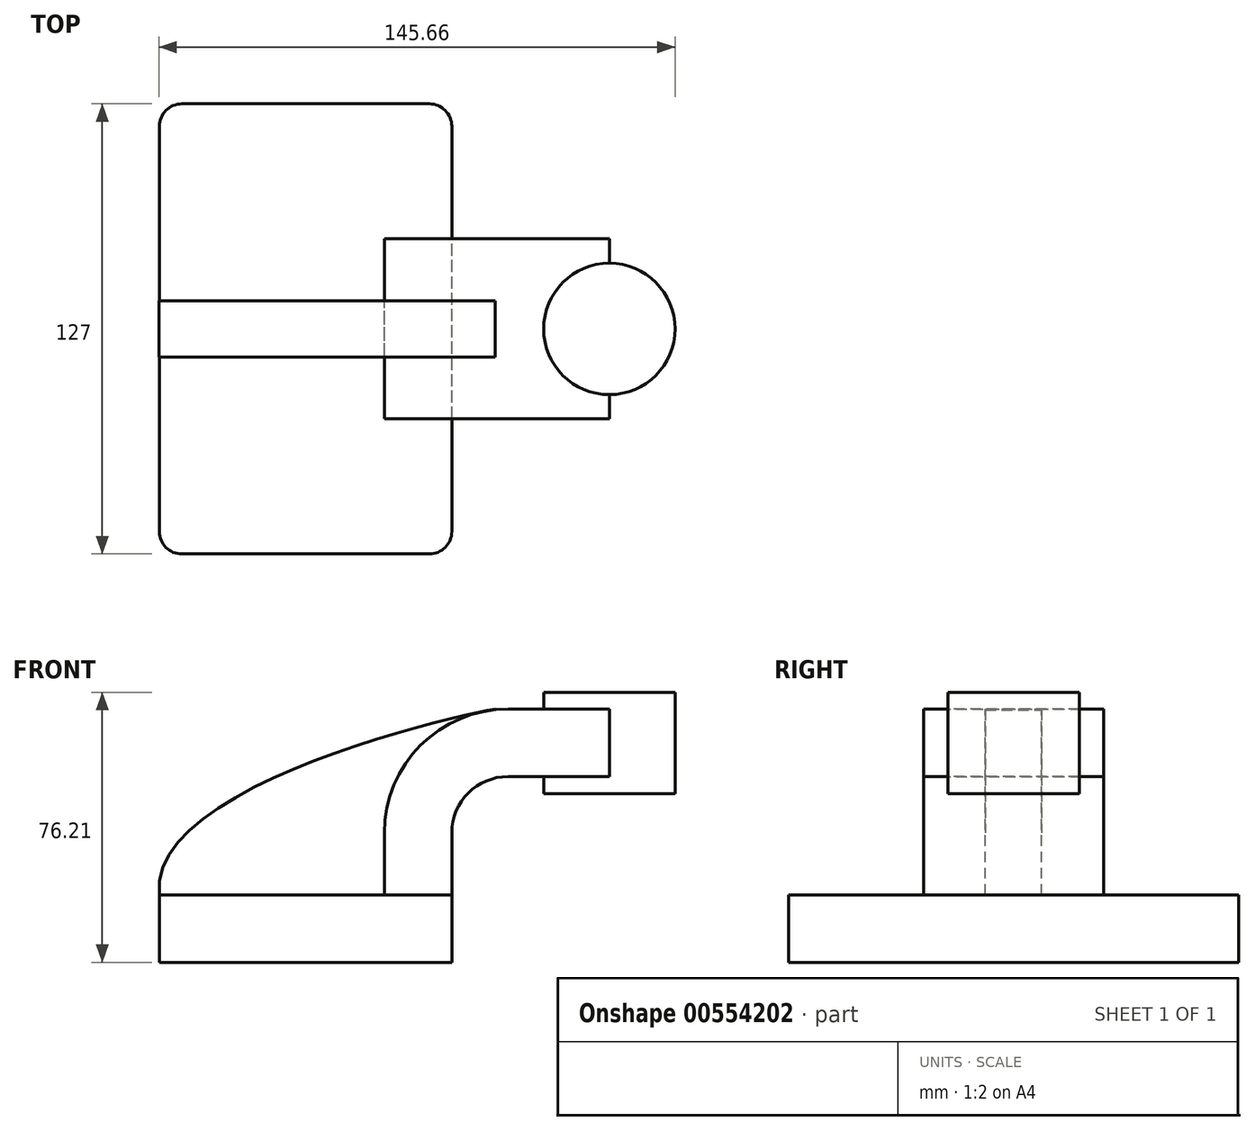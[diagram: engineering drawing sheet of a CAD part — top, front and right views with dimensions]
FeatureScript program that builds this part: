
annotation { "Feature Type Name" : "Feature", "Feature Type Description" : "" }
export const myFeature = defineFeature(function(context is Context, id is Id, definition is map)
    precondition{}
    {
        {
            var Q0;
            Q0=qCreatedBy(makeId("Front.planeOp"),FACE);
            var sketch = newSketch(context, id + "F0", { "sketchPlane" : qUnion([Q0])});
            skLineSegment(sketch, "E0.bottom", {"start": v(-41.28, 9.52) * mm, "end": v(41.27, 9.53) * mm});
            skLineSegment(sketch, "E0.top", {"start": v(-41.28, -9.53) * mm, "end": v(41.28, -9.53) * mm});
            skLineSegment(sketch, "E0.left", {"start": v(-41.28, 9.52) * mm, "end": v(-41.28, -9.53) * mm});
            skLineSegment(sketch, "E0.right", {"start": v(41.27, 9.53) * mm, "end": v(41.28, -9.52) * mm});
            skPoint(sketch, "E0.middle", {"position": v(0, 0) * mm});
            skLineSegment(sketch, "E1.bottom", {"start": v(104.27, 38.1) * mm, "end": v(53.47, 38.1) * mm});
            skLineSegment(sketch, "E1.top", {"start": v(104.27, 66.67) * mm, "end": v(53.47, 66.67) * mm});
            skLineSegment(sketch, "E1.left", {"start": v(104.27, 38.1) * mm, "end": v(104.27, 66.67) * mm});
            skLineSegment(sketch, "E1.right", {"start": v(53.47, 38.1) * mm, "end": v(53.47, 66.67) * mm});
            skPoint(sketch, "E1.middle", {"position": v(78.87, 52.39) * mm});
            skLineSegment(sketch, "E2", {"start": v(41.27, 9.53) * mm, "end": v(41.27, 27) * mm});
            skArc(sketch, "E3", {"start": v(41.27, 27) * mm, "mid": v(45.92, 38.23) * mm, "end": v(57.15, 42.88) * mm});
            skLineSegment(sketch, "E4", {"start": v(57.15, 42.88) * mm, "end": v(85.72, 42.88) * mm});
            skLineSegment(sketch, "E5.0", {"start": v(57.15, 61.93) * mm, "end": v(85.72, 61.93) * mm});
            skArc(sketch, "E5.1", {"start": v(22.22, 27) * mm, "mid": v(32.45, 51.7) * mm, "end": v(57.15, 61.93) * mm});
            skLineSegment(sketch, "E5.2", {"start": v(22.22, 9.53) * mm, "end": v(22.22, 27) * mm});
            skLineSegment(sketch, "E6", {"start": v(85.72, 42.88) * mm, "end": v(85.72, 61.93) * mm});
            skFitSpline(sketch, "E7", {"points": [v(-41.28, 9.52) * mm, v(53.47, 61.93) * mm, v(57.15, 61.93) * mm], "startDerivative": vector(-12.96, 107.01) * mm, "endDerivative": vector(16.74, -4.83) * mm});
            skLineSegment(sketch, "E8", {"start": v(85.72, 42.88) * mm, "end": v(85.72, 38.1) * mm});
            skPoint(sketch, "E8.endSnap0", {"position": v(78.87, 38.1) * mm});
            skLineSegment(sketch, "E9", {"start": v(85.72, 61.93) * mm, "end": v(85.72, 66.67) * mm});
            skSolve(sketch);
        }
        {
            var Q0;
            Q0=makeQuery(id+"F0.imprint","IMPRINT",FACE,{"disambiguationData":[TD([[makeQuery(id+"F0.imprint","IMPRINT",EDGE,{"derivedFrom":sQuery(id+"F0.wireOp",EDGE,"E0.top")}),1.0]])]});
            extrude(context, id + "F1", {"entities" : qUnion([Q0]), "endBound" : BoundingType.SYMMETRIC, "depth" : 127 * mm, "offsetDistance" : 25.4 * mm});
        }
        {
            var Q0;
            {var subQ1=sQuery(id+"F0.wireOp",EDGE,"E2");Q0=makeQuery(id+"F0.imprint","IMPRINT",FACE,{"disambiguationData":[TD([[makeQuery(id+"F0.imprint","IMPRINT",EDGE,{"derivedFrom":subQ1}),1.0]])]});}
            var Q1;
            {var subQ1=sQuery(id+"F0.wireOp",EDGE,"E4");Q1=makeQuery(id+"F0.imprint","IMPRINT",FACE,{"disambiguationData":[TD([[makeQuery(id+"F0.imprint","IMPRINT",EDGE,{"derivedFrom":subQ1}),1.0]])]});}
            extrude(context, id + "F2", {"entities" : qUnion([Q0, Q1]), "endBound" : BoundingType.SYMMETRIC, "depth" : 50.8 * mm, "offsetDistance" : 25.4 * mm});
        }
        {
            var Q0;
            {var subQ0=sQuery(id+"F0.wireOp",EDGE,"E5.2");Q0=makeQuery(id+"F0.imprint","IMPRINT",FACE,{"disambiguationData":[TD([[makeQuery(id+"F0.imprint","IMPRINT",EDGE,{"derivedFrom":subQ0}),1.0]])]});}
            extrude(context, id + "F3", {"entities" : qUnion([Q0]), "endBound" : BoundingType.SYMMETRIC, "depth" : 15.88 * mm, "offsetDistance" : 25.4 * mm});
        }
        {
            var Q0;
            {var subQ0=sQuery(id+"F0.wireOp",EDGE,"E1.left");Q0=makeQuery(id+"F0.imprint","IMPRINT",FACE,{"disambiguationData":[TD([[makeQuery(id+"F0.imprint","IMPRINT",EDGE,{"derivedFrom":subQ0}),1.0]])]});}
            var Q1;
            Q1=sQuery(id+"F0.wireOp",EDGE,"E6");
            revolve(context, id + "F4", {"operationType" : NewBodyOperationType.ADD, "entities" : qUnion([Q0]), "axis" : qUnion([Q1]), "revolveType" : RevolveType.FULL});
        }
        {
            var Q0;
            Q0=makeQuery(id+"F1.opExtrude","CAP_EDGE",EDGE,{"disambiguationData":[OSD([sQuery(id+"F0.wireOp",EDGE,"E0.left")])],"isStart":false});
            var Q1;
            Q1=makeQuery(id+"F1.opExtrude","CAP_EDGE",EDGE,{"disambiguationData":[OSD([sQuery(id+"F0.wireOp",EDGE,"E0.right")])],"isStart":false});
            var Q2;
            Q2=makeQuery(id+"F1.opExtrude","CAP_EDGE",EDGE,{"disambiguationData":[OSD([sQuery(id+"F0.wireOp",EDGE,"E0.right")])],"isStart":true});
            var Q3;
            Q3=makeQuery(id+"F1.opExtrude","CAP_EDGE",EDGE,{"disambiguationData":[OSD([sQuery(id+"F0.wireOp",EDGE,"E0.left")])],"isStart":true});
            fillet(context, id + "F5", {"entities" : qUnion([Q0, Q1, Q2, Q3]), "radius" : 6.35 * mm, "tangentPropagation" : true, "allowEdgeOverflow" : false});
        }
    });
